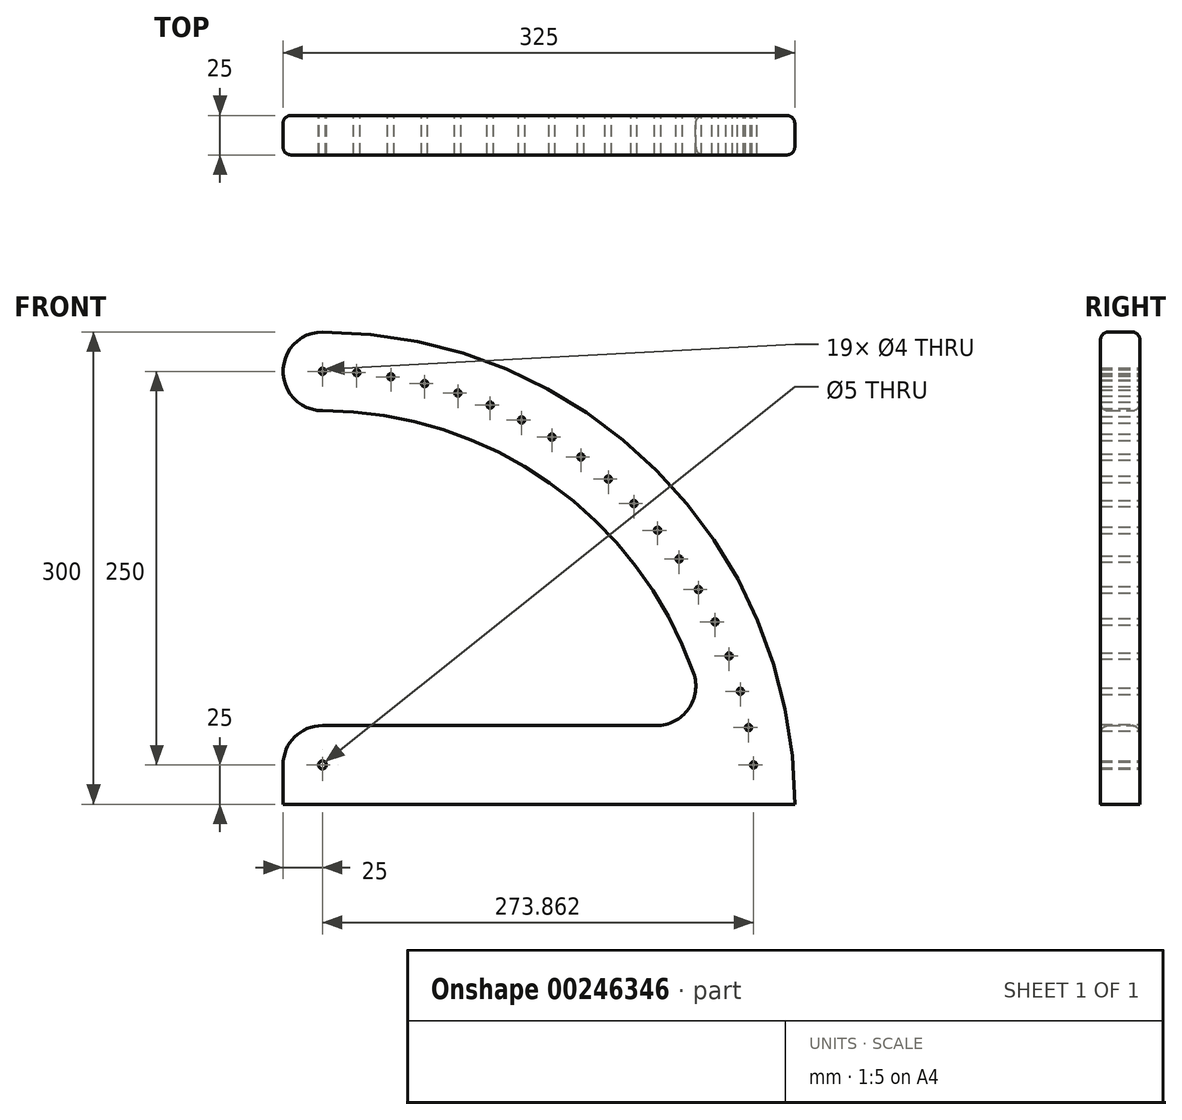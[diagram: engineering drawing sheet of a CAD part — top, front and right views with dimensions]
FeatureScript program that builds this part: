
annotation { "Feature Type Name" : "Feature", "Feature Type Description" : "" }
export const myFeature = defineFeature(function(context is Context, id is Id, definition is map)
    precondition{}
    {
        {
            var Q0;
            Q0=qCreatedBy(makeId("Front.planeOp"),FACE);
            var sketch = newSketch(context, id + "F0", { "sketchPlane" : qUnion([Q0])});
            skArc(sketch, "E0", {"start": v(300, 0) * mm, "mid": v(212.13, 212.13) * mm, "end": v(0, 300) * mm});
            skArc(sketch, "E1", {"start": v(235.7, 83.33) * mm, "mid": v(144.34, 204.12) * mm, "end": v(0, 250) * mm});
            skArc(sketch, "E2", {"start": v(0, 300) * mm, "mid": v(-25, 275) * mm, "end": v(0, 250) * mm});
            skPoint(sketch, "E3.endSnap0", {"position": v(-25, 275) * mm});
            skPoint(sketch, "E4.visualSharp", {"position": v(244.95, 50) * mm});
            skArc(sketch, "E4.filletArc", {"start": v(212.13, 50) * mm, "mid": v(232.54, 60.57) * mm, "end": v(235.7, 83.33) * mm});
            skLineSegment(sketch, "E5", {"start": v(212.13, 50) * mm, "end": v(-25, 50) * mm});
            skLineSegment(sketch, "E6", {"start": v(300, 0) * mm, "end": v(-25, 0) * mm});
            skLineSegment(sketch, "E7", {"start": v(-25, 0) * mm, "end": v(-25, 50) * mm});
            skCircle(sketch, "E8", {"center": v(0, 275) * mm, "radius": 2 * mm});
            skCircle(sketch, "E9", {"center": v(21.8, 274.13) * mm, "radius": 2 * mm});
            skCircle(sketch, "E10", {"center": v(43.47, 271.54) * mm, "radius": 2 * mm});
            skCircle(sketch, "E11", {"center": v(64.9, 267.23) * mm, "radius": 2 * mm});
            skCircle(sketch, "E12", {"center": v(85.98, 261.21) * mm, "radius": 2 * mm});
            skCircle(sketch, "E13", {"center": v(106.56, 253.52) * mm, "radius": 2 * mm});
            skCircle(sketch, "E14", {"center": v(126.53, 244.16) * mm, "radius": 2 * mm});
            skCircle(sketch, "E15", {"center": v(145.77, 233.19) * mm, "radius": 2 * mm});
            skCircle(sketch, "E16", {"center": v(164.15, 220.63) * mm, "radius": 2 * mm});
            skCircle(sketch, "E17", {"center": v(181.55, 206.55) * mm, "radius": 2 * mm});
            skCircle(sketch, "E18", {"center": v(197.84, 191) * mm, "radius": 2 * mm});
            skCircle(sketch, "E19", {"center": v(212.9, 174.07) * mm, "radius": 2 * mm});
            skCircle(sketch, "E20", {"center": v(226.6, 155.82) * mm, "radius": 2 * mm});
            skCircle(sketch, "E21", {"center": v(238.81, 136.36) * mm, "radius": 2 * mm});
            skCircle(sketch, "E22", {"center": v(249.39, 115.9) * mm, "radius": 2 * mm});
            skCircle(sketch, "E23", {"center": v(258.35, 94.23) * mm, "radius": 2 * mm});
            skCircle(sketch, "E24", {"center": v(265.46, 71.8) * mm, "radius": 2 * mm});
            skCircle(sketch, "E25", {"center": v(270.66, 48.68) * mm, "radius": 2 * mm});
            skCircle(sketch, "E26", {"center": v(0, 25) * mm, "radius": 2.5 * mm});
            skPoint(sketch, "E26.centerSnap0", {"position": v(-25, 25) * mm});
            skCircle(sketch, "E27", {"center": v(273.86, 25) * mm, "radius": 2 * mm});
            skSolve(sketch);
        }
        {
            var Q0;
            Q0 = qSketchRegion(id + "F0", true);
            extrude(context, id + "F1", {"entities" : qUnion([Q0]), "depth" : 25 * mm});
        }
        {
            var Q0;
            Q0=makeQuery(id+"F1.opExtrude","CAP_EDGE",EDGE,{"disambiguationData":[OSD([sQuery(id+"F0.wireOp",EDGE,"E5")])],"isStart":false});
            var Q1;
            Q1=makeQuery(id+"F1.opExtrude","CAP_EDGE",EDGE,{"disambiguationData":[OSD([sQuery(id+"F0.wireOp",EDGE,"E7")])],"isStart":false});
            var Q2;
            Q2=makeQuery(id+"F1.opExtrude","CAP_EDGE",EDGE,{"disambiguationData":[OSD([sQuery(id+"F0.wireOp",EDGE,"E5")])],"isStart":true});
            var Q3;
            Q3=makeQuery(id+"F1.opExtrude","CAP_EDGE",EDGE,{"disambiguationData":[OSD([sQuery(id+"F0.wireOp",EDGE,"E7")])],"isStart":true});
            fillet(context, id + "F2", {"entities" : qUnion([Q0, Q1, Q2, Q3]), "radius" : 5 * mm, "tangentPropagation" : true, "allowEdgeOverflow" : false});
        }
        {
            var Q0;
            Q0=makeQuery(id+"F1.opExtrude","SWEPT_EDGE",EDGE,{"disambiguationData":[OSD([sQuery(id+"F0.wireOp",EDGE,"E5"),sQuery(id+"F0.wireOp",EDGE,"E7")])]});
            fillet(context, id + "F3", {"entities" : qUnion([Q0]), "radius" : 25 * mm, "tangentPropagation" : true, "allowEdgeOverflow" : false});
        }
    });
